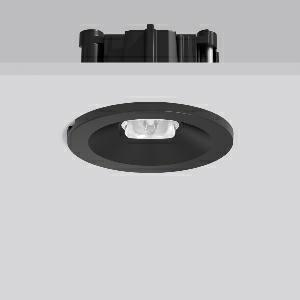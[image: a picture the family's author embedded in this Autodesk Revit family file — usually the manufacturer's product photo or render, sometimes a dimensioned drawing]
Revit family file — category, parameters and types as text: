
# Revit family: turia_l_672414_003_89_f510
name_source: partatom
category: Lighting Fixtures
units: mm (PartAtom-declared; Revit-internal decimal feet)

## family parameters
Cut with Voids When Loaded = No
Host = Face
Light Source = No
Part Type = Normal
Room Calculation Point = No
Round Connector Dimension = Use Diameter
Shared = No

## types (1)
- TURIA L (1 x LED Modul 765, 200 lm, 6500)
    Apparent Load = 5 VA
    CIE Flux Codes = 35 70 99 100 100
    Color Rendering = 70
    Color Temperature = 6500
    Default Elevation = 1800 mm
    Description = Series: TURIA L
Round emergency luminaire for escape route lighting. With plastic lenses for escape route illumination. Suitable for connection to central battery systems. With MOM monitoring module for LPS (Low Power Supply) small central battery units of the type Easy+IP. With enclosed separate ceiling mounting ring also suitable for ceiling cut-outs of Ø 68 mm. 
Colour: black
Diameter: 62 mm
Height: 3 mm
Cut-out diameter: 54-68 mm
Recess height: 76-162 mm
Luminaire: recess height: 42 mm
Weight: 350 g
Operating mode: non-maintained power mode
Lamp: LED
Socket: without socket
Colour temperature: 6500K
Colour rendering index (CRI): 70
System power: 4.8 W
Rated luminous flux: 200 lm
Luminous flux, emergency: 200 lm
System power, emergency: 4.8 W
Control gear: Regulated power supply
Protection class: II
Type of protection: IP 20
    Height = 0 mm  [stored 0 ft]
    Lamp = 1 x LED Modul 765
    Lamp Light Flux = 200 lm
    Lamp count = 1
    Length = 62 mm  [stored 0.203412 ft]
    Lifetime = 50000 h
    Luminous efficacy = 42 lm/W
    Manufacturer = RZB
    ModVariant = No
    Model = 672414.003.89
    Mounting Place = Ceiling
    Mounting Type = Recessed
    Number of Poles = 1
    OnlyDefault = Yes
    Power Factor = 1
    Product Name = TURIA L
    Product group = Recessed ceiling luminaires
    ProductGroupID = 405
    Protection Class = Protection class II
    Protection Degree = IP 20
    RLX_Detail_Level = 1
    RLX_Emergency_Light_Flux = 200 lm
    RLX_Emergency_Type = 3
    RLX_Emergency_Type_DB = Yes
    RlxData = <blob elided: 57873 chars, md5=eda88550>
    Socket = socket
    Standby Power = 0 W
    System Light Flux = 200 lm
    System Power = 5 W
    Type Comments = Product without accessories
    Type Image = 672414.003.jpg
    URL = http://relux.com
    VarID = ---
    Voltage = 230 V
    Voltage Range = 220-240 V
    Weight = 0.00 kg
    Width = 0 mm  [stored 0 ft]

note: [stored X ft] marks values corroborated as IEEE doubles in the binary element streams (Revit-internal decimal feet)

## geometry (parser evidence)
native form markers: Blend x4, Sweep x12
no freeform markers — native parametric forms only
